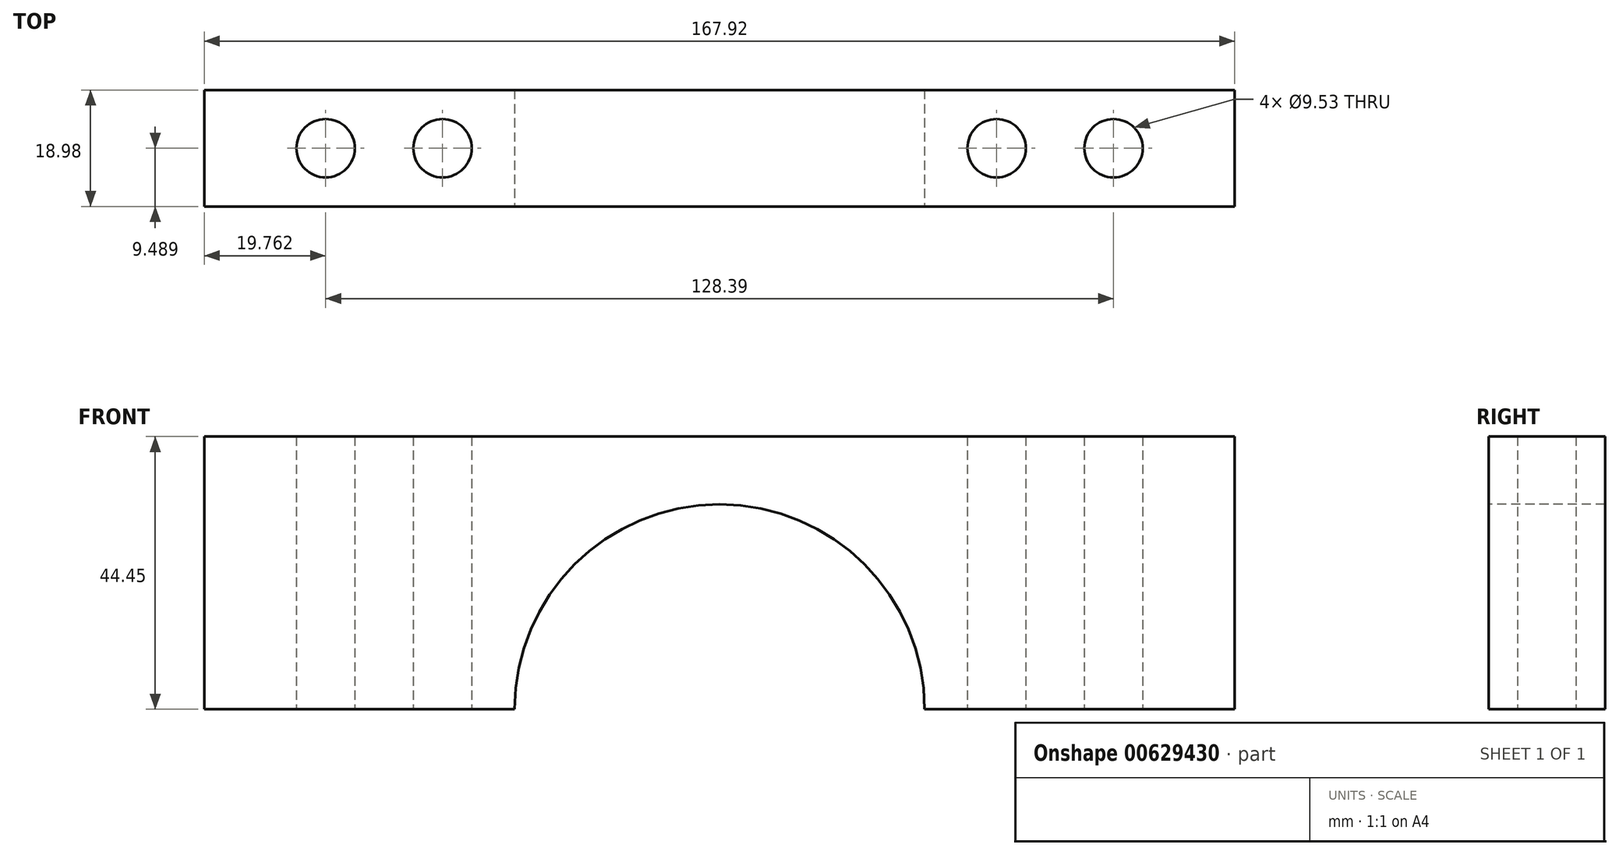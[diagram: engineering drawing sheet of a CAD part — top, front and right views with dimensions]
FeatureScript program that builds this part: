
annotation { "Feature Type Name" : "Feature", "Feature Type Description" : "" }
export const myFeature = defineFeature(function(context is Context, id is Id, definition is map)
    precondition{}
    {
        {
            var Q0;
            Q0=qCreatedBy(makeId("Top.planeOp"),FACE);
            var sketch = newSketch(context, id + "F0", { "sketchPlane" : qUnion([Q0])});
            skCircle(sketch, "E0", {"center": v(-111.03, -59.4) * mm, "radius": 4.76 * mm});
            skCircle(sketch, "E1", {"center": v(-130.08, -59.4) * mm, "radius": 4.76 * mm});
            skCircle(sketch, "E2.MirrorC", {"center": v(-1.69, -59.4) * mm, "radius": 4.76 * mm});
            skCircle(sketch, "E3.MirrorC", {"center": v(-20.74, -59.4) * mm, "radius": 4.76 * mm});
            skLineSegment(sketch, "E4", {"start": v(-130.08, -59.4) * mm, "end": v(-1.69, -59.4) * mm, "construction": true});
            skLineSegment(sketch, "E5.bottom", {"start": v(-149.84, -49.91) * mm, "end": v(18.08, -49.91) * mm});
            skLineSegment(sketch, "E5.top", {"start": v(-149.84, -68.89) * mm, "end": v(18.08, -68.89) * mm});
            skLineSegment(sketch, "E5.left", {"start": v(-149.84, -49.91) * mm, "end": v(-149.84, -68.89) * mm});
            skLineSegment(sketch, "E5.right", {"start": v(18.08, -49.91) * mm, "end": v(18.08, -68.89) * mm});
            skPoint(sketch, "E5.middle", {"position": v(-65.88, -59.4) * mm});
            skSolve(sketch);
        }
        {
            var Q0;
            Q0=makeQuery(id+"F0.imprint","IMPRINT",FACE,{"disambiguationData":[TD([[makeQuery(id+"F0.imprint","IMPRINT",EDGE,{"derivedFrom":sQuery(id+"F0.wireOp",EDGE,"E0")}),-1.0]])]});
            extrude(context, id + "F1", {"entities" : qUnion([Q0]), "depth" : 44.45 * mm, "offsetDistance" : 25.4 * mm});
        }
        {
            var Q0;
            Q0=makeQuery(id+"F1.opExtrude","SWEPT_FACE",FACE,{"disambiguationData":[OSD([sQuery(id+"F0.wireOp",EDGE,"E5.top")])]});
            var sketch = newSketch(context, id + "F2", { "sketchPlane" : qUnion([Q0])});
            skCircle(sketch, "E6", {"center": v(-65.88, 0) * mm, "radius": 33.4 * mm});
            skSolve(sketch);
        }
        {
            var Q0;
            {var subQ0=sQuery(id+"F2.wireOp",EDGE,"E6");var subQ1=makeQuery(id+"F1.opExtrude","CAP_EDGE",EDGE,{"disambiguationData":[OSD([sQuery(id+"F0.wireOp",EDGE,"E5.top")])],"isStart":true});var subQ2=makeQuery(id+"F2.imprint","INTERSECT",VERTEX,{"disambiguationData":[OD(0.0)],"derivedFrom":[subQ1,subQ0]});Q0=makeQuery(id+"F2.imprint","IMPRINT",FACE,{"disambiguationData":[TD([[makeQuery(id+"F2.imprint","IMPRINT",EDGE,{"disambiguationData":[TD([[subQ2,1.0]])],"derivedFrom":subQ0}),1.0]])]});}
            extrude(context, id + "F3", {"entities" : qUnion([Q0]), "operationType" : NewBodyOperationType.REMOVE, "oppositeDirection" : true, "depth" : 25.4 * mm, "offsetDistance" : 25.4 * mm});
        }
    });
